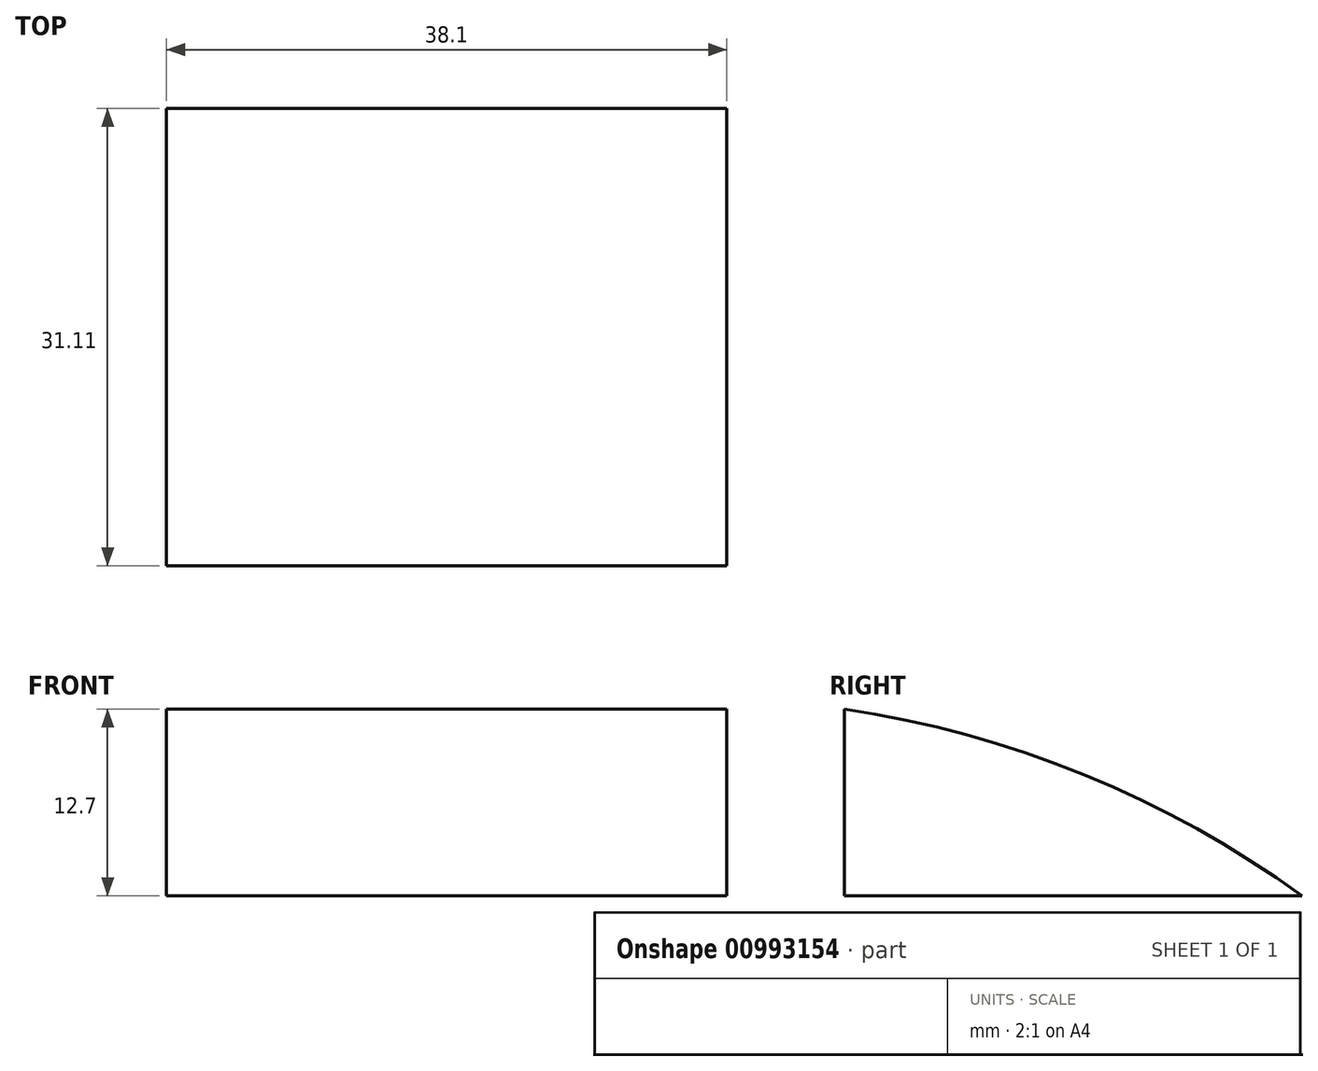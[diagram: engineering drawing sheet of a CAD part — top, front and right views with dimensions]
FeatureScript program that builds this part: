
annotation { "Feature Type Name" : "Feature", "Feature Type Description" : "" }
export const myFeature = defineFeature(function(context is Context, id is Id, definition is map)
    precondition{}
    {
        {
            var Q0;
            Q0=qCreatedBy(makeId("Right.planeOp"),FACE);
            var sketch = newSketch(context, id + "F0", { "sketchPlane" : qUnion([Q0])});
            skLineSegment(sketch, "E0", {"start": v(-46.57, 36.84) * mm, "end": v(15.66, 36.84) * mm});
            skArc(sketch, "E1", {"start": v(15.66, 36.84) * mm, "mid": v(0.87, 45.07) * mm, "end": v(-15.45, 49.54) * mm});
            skPoint(sketch, "E1.endSnap0", {"position": v(-15.45, 36.84) * mm});
            skLineSegment(sketch, "E2.bottom", {"start": v(-46.57, 36.84) * mm, "end": v(-15.45, 36.84) * mm});
            skLineSegment(sketch, "E2.top", {"start": v(-46.57, 49.54) * mm, "end": v(-15.45, 49.54) * mm});
            skLineSegment(sketch, "E2.left", {"start": v(-46.57, 36.84) * mm, "end": v(-46.57, 49.54) * mm});
            skLineSegment(sketch, "E2.right", {"start": v(-15.45, 36.84) * mm, "end": v(-15.45, 49.54) * mm});
            skSolve(sketch);
        }
        {
            var Q0;
            Q0=makeQuery(id+"F0.imprint","IMPRINT",FACE,{"disambiguationData":[TD([[makeQuery(id+"F0.imprint","IMPRINT",EDGE,{"derivedFrom":sQuery(id+"F0.wireOp",EDGE,"E2.bottom")}),1.0]])]});
            var Q1;
            Q1=makeQuery(id+"F0.imprint","IMPRINT",FACE,{"disambiguationData":[TD([[makeQuery(id+"F0.imprint","IMPRINT",EDGE,{"derivedFrom":sQuery(id+"F0.wireOp",EDGE,"E0")}),1.0]])]});
            extrude(context, id + "F1", {"entities" : qUnion([Q0, Q1]), "depth" : 38.1 * mm, "offsetDistance" : 25.4 * mm});
        }
        {
            var Q0;
            Q0=makeQuery(id+"F1.opExtrude","SWEPT_FACE",FACE,{"disambiguationData":[OSD([sQuery(id+"F0.wireOp",EDGE,"E0"),sQuery(id+"F0.wireOp",EDGE,"E2.bottom")])]});
            var sketch = newSketch(context, id + "F2", { "sketchPlane" : qUnion([Q0])});
            skPoint(sketch, "E3.firstSnap0", {"position": v(38.1, 15.45) * mm});
            skLineSegment(sketch, "E3.bottom", {"start": v(30.48, 15.45) * mm, "end": v(7.62, 15.45) * mm});
            skLineSegment(sketch, "E3.top", {"start": v(30.48, 46.57) * mm, "end": v(7.62, 46.57) * mm});
            skLineSegment(sketch, "E3.left", {"start": v(30.48, 15.45) * mm, "end": v(30.48, 46.57) * mm});
            skLineSegment(sketch, "E3.right", {"start": v(7.62, 15.45) * mm, "end": v(7.62, 46.57) * mm});
            skSolve(sketch);
        }
        {
            var Q0;
            Q0=makeQuery(id+"F2.imprint","IMPRINT",FACE,{"disambiguationData":[TD([[makeQuery(id+"F2.imprint","IMPRINT",EDGE,{"derivedFrom":sQuery(id+"F2.wireOp",EDGE,"E3.bottom")}),-1.0]])]});
            extrude(context, id + "F3", {"entities" : qUnion([Q0]), "operationType" : NewBodyOperationType.REMOVE, "oppositeDirection" : true, "depth" : 5.08 * mm, "offsetDistance" : 25.4 * mm});
        }
    });
